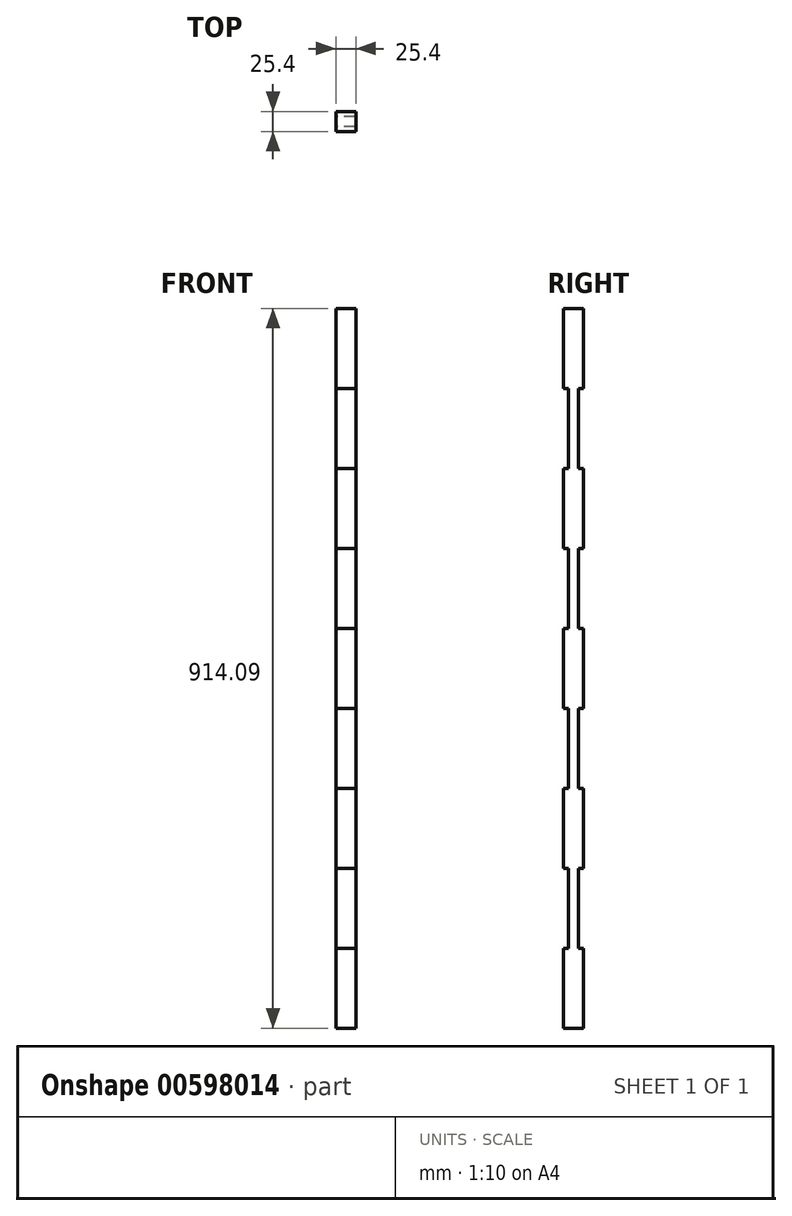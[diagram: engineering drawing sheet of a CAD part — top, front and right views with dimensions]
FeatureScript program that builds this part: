
annotation { "Feature Type Name" : "Feature", "Feature Type Description" : "" }
export const myFeature = defineFeature(function(context is Context, id is Id, definition is map)
    precondition{}
    {
        {
            var Q0;
            Q0=qCreatedBy(makeId("Right.planeOp"),FACE);
            var sketch = newSketch(context, id + "F0", { "sketchPlane" : qUnion([Q0])});
            skLineSegment(sketch, "E0", {"start": v(-12.7, 355.57) * mm, "end": v(-12.7, 457.17) * mm});
            skLineSegment(sketch, "E1", {"start": v(-12.7, 457.17) * mm, "end": v(0, 457.17) * mm});
            skLineSegment(sketch, "E2", {"start": v(0, 457.17) * mm, "end": v(0, -456.92) * mm});
            skLineSegment(sketch, "E3", {"start": v(0, -456.92) * mm, "end": v(-12.7, -456.92) * mm});
            skLineSegment(sketch, "E4", {"start": v(-12.7, -456.92) * mm, "end": v(-12.7, -355.58) * mm});
            skLineSegment(sketch, "E5", {"start": v(-12.7, -355.58) * mm, "end": v(-6.35, -355.58) * mm});
            skLineSegment(sketch, "E6", {"start": v(-6.35, -355.58) * mm, "end": v(-6.35, -254.03) * mm});
            skLineSegment(sketch, "E7", {"start": v(-6.35, -254.03) * mm, "end": v(-12.7, -254.03) * mm});
            skLineSegment(sketch, "E8", {"start": v(-12.7, -254.03) * mm, "end": v(-12.7, -152.43) * mm});
            skLineSegment(sketch, "E9", {"start": v(-12.7, -152.43) * mm, "end": v(-6.35, -152.43) * mm});
            skLineSegment(sketch, "E10", {"start": v(-6.35, -152.43) * mm, "end": v(-6.35, -50.83) * mm});
            skLineSegment(sketch, "E11", {"start": v(-6.35, -50.83) * mm, "end": v(-12.7, -50.83) * mm});
            skLineSegment(sketch, "E12", {"start": v(-12.7, -50.83) * mm, "end": v(-12.7, 50.77) * mm});
            skLineSegment(sketch, "E13", {"start": v(-12.7, 50.77) * mm, "end": v(-6.35, 50.77) * mm});
            skLineSegment(sketch, "E14", {"start": v(-6.35, 50.77) * mm, "end": v(-6.35, 152.37) * mm});
            skLineSegment(sketch, "E15", {"start": v(-6.35, 152.37) * mm, "end": v(-12.7, 152.37) * mm});
            skLineSegment(sketch, "E16", {"start": v(-12.7, 152.37) * mm, "end": v(-12.7, 253.97) * mm});
            skLineSegment(sketch, "E17", {"start": v(-12.7, 253.97) * mm, "end": v(-6.35, 253.97) * mm});
            skLineSegment(sketch, "E18", {"start": v(-6.35, 253.97) * mm, "end": v(-6.35, 355.57) * mm});
            skLineSegment(sketch, "E19", {"start": v(-6.35, 355.57) * mm, "end": v(-12.7, 355.57) * mm});
            skLineSegment(sketch, "E20.MirrorCS", {"start": v(12.7, 457.17) * mm, "end": v(0, 457.17) * mm});
            skLineSegment(sketch, "E21.MirrorCS", {"start": v(12.7, 355.57) * mm, "end": v(12.7, 457.17) * mm});
            skLineSegment(sketch, "E22.MirrorCS", {"start": v(6.35, 355.57) * mm, "end": v(12.7, 355.57) * mm});
            skLineSegment(sketch, "E23.MirrorCS", {"start": v(6.35, 253.97) * mm, "end": v(6.35, 355.57) * mm});
            skLineSegment(sketch, "E24.MirrorCS", {"start": v(12.7, 253.97) * mm, "end": v(6.35, 253.97) * mm});
            skLineSegment(sketch, "E25.MirrorCS", {"start": v(12.7, 152.37) * mm, "end": v(12.7, 253.97) * mm});
            skLineSegment(sketch, "E26.MirrorCS", {"start": v(6.35, 152.37) * mm, "end": v(12.7, 152.37) * mm});
            skLineSegment(sketch, "E27.MirrorCS", {"start": v(6.35, 50.77) * mm, "end": v(6.35, 152.37) * mm});
            skLineSegment(sketch, "E28.MirrorCS", {"start": v(12.7, 50.77) * mm, "end": v(6.35, 50.77) * mm});
            skLineSegment(sketch, "E29.MirrorCS", {"start": v(12.7, -50.83) * mm, "end": v(12.7, 50.77) * mm});
            skLineSegment(sketch, "E30.MirrorCS", {"start": v(6.35, -50.83) * mm, "end": v(12.7, -50.83) * mm});
            skLineSegment(sketch, "E31.MirrorCS", {"start": v(6.35, -152.43) * mm, "end": v(6.35, -50.83) * mm});
            skLineSegment(sketch, "E32.MirrorCS", {"start": v(12.7, -152.43) * mm, "end": v(6.35, -152.43) * mm});
            skLineSegment(sketch, "E33.MirrorCS", {"start": v(12.7, -254.03) * mm, "end": v(12.7, -152.43) * mm});
            skLineSegment(sketch, "E34.MirrorCS", {"start": v(6.35, -254.03) * mm, "end": v(12.7, -254.03) * mm});
            skLineSegment(sketch, "E35.MirrorCS", {"start": v(6.35, -355.58) * mm, "end": v(6.35, -254.03) * mm});
            skLineSegment(sketch, "E36.MirrorCS", {"start": v(12.7, -355.58) * mm, "end": v(6.35, -355.58) * mm});
            skLineSegment(sketch, "E37.MirrorCS", {"start": v(12.7, -456.92) * mm, "end": v(12.7, -355.58) * mm});
            skLineSegment(sketch, "E38.MirrorCS", {"start": v(0, -456.92) * mm, "end": v(12.7, -456.92) * mm});
            skSolve(sketch);
        }
        {
            var Q0;
            Q0=makeQuery(id+"F0.imprint","IMPRINT",FACE,{"disambiguationData":[TD([[makeQuery(id+"F0.imprint","IMPRINT",EDGE,{"derivedFrom":sQuery(id+"F0.wireOp",EDGE,"E0")}),-1.0]])]});
            var Q1;
            Q1=makeQuery(id+"F0.imprint","IMPRINT",FACE,{"disambiguationData":[TD([[makeQuery(id+"F0.imprint","IMPRINT",EDGE,{"derivedFrom":sQuery(id+"F0.wireOp",EDGE,"E2")}),1.0]])]});
            extrude(context, id + "F1", {"entities" : qUnion([Q0, Q1]), "depth" : 25.4 * mm, "offsetDistance" : 25.4 * mm});
        }
    });
